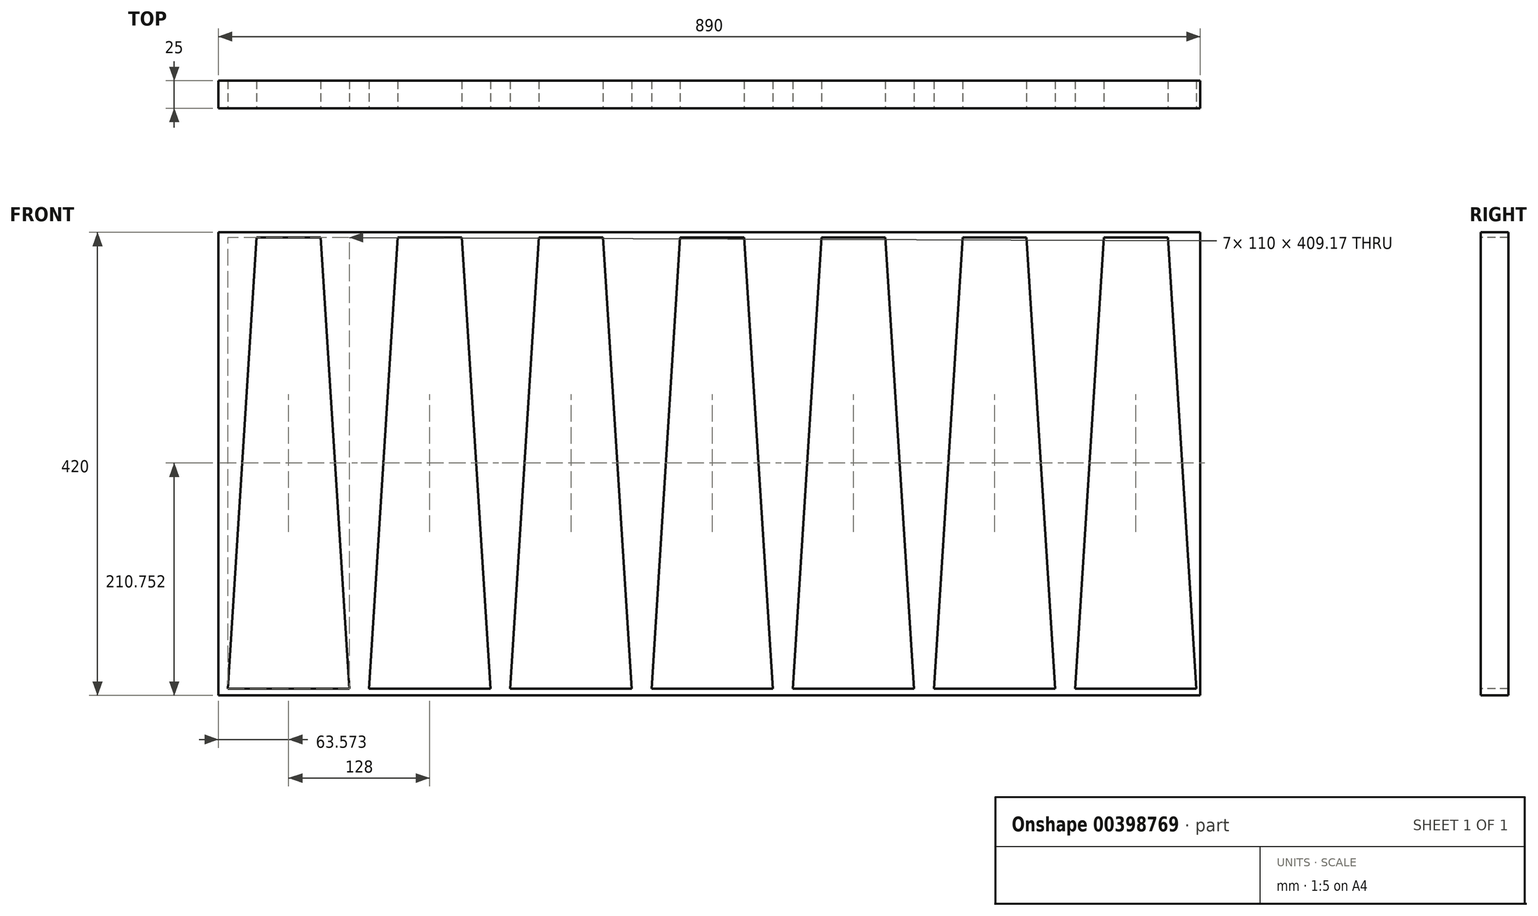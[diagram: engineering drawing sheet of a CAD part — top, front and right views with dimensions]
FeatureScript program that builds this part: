
annotation { "Feature Type Name" : "Feature", "Feature Type Description" : "" }
export const myFeature = defineFeature(function(context is Context, id is Id, definition is map)
    precondition{}
    {
        {
            var Q0;
            Q0=qCreatedBy(makeId("Front.planeOp"),FACE);
            var sketch = newSketch(context, id + "F0", { "sketchPlane" : qUnion([Q0])});
            skLineSegment(sketch, "E0.bottom", {"start": v(445, -210) * mm, "end": v(-445, -210) * mm});
            skLineSegment(sketch, "E0.top", {"start": v(445, 210) * mm, "end": v(-445, 210) * mm});
            skLineSegment(sketch, "E0.left", {"start": v(445, -210) * mm, "end": v(445, 210) * mm});
            skLineSegment(sketch, "E0.right", {"start": v(-445, -210) * mm, "end": v(-445, 210) * mm});
            skPoint(sketch, "E0.middle", {"position": v(0, 0) * mm});
            skSolve(sketch);
        }
        {
            var Q0;
            Q0 = qSketchRegion(id + "F0", true);
            extrude(context, id + "F1", {"entities" : qUnion([Q0]), "depth" : 25 * mm});
        }
        {
            var Q0;
            Q0=makeQuery(id+"F1.opExtrude","CAP_FACE",FACE,{"disambiguationData":[OSD([sQuery(id+"F0.wireOp",EDGE,"E0.bottom"),sQuery(id+"F0.wireOp",EDGE,"E0.top"),sQuery(id+"F0.wireOp",EDGE,"E0.left"),sQuery(id+"F0.wireOp",EDGE,"E0.right")])],"isStart":false});
            var sketch = newSketch(context, id + "F2", { "sketchPlane" : qUnion([Q0])});
            skLineSegment(sketch, "E1", {"start": v(-381.43, -203.83) * mm, "end": v(-326.43, -203.83) * mm});
            skLineSegment(sketch, "E2", {"start": v(-326.43, -203.83) * mm, "end": v(-352.43, 205.34) * mm});
            skLineSegment(sketch, "E3", {"start": v(-352.43, 205.34) * mm, "end": v(-381.43, 205.34) * mm});
            skLineSegment(sketch, "E4", {"start": v(-381.43, 143.69) * mm, "end": v(-381.43, -293.33) * mm, "construction": true});
            skLineSegment(sketch, "E5.MirrorCS", {"start": v(-410.43, 205.34) * mm, "end": v(-381.43, 205.34) * mm});
            skLineSegment(sketch, "E6.MirrorCS", {"start": v(-436.43, -203.83) * mm, "end": v(-410.43, 205.34) * mm});
            skLineSegment(sketch, "E7.MirrorCS", {"start": v(-381.43, -203.83) * mm, "end": v(-436.43, -203.83) * mm});
            skLineSegment(sketch, "E8.1.0.0", {"start": v(-253.43, 143.69) * mm, "end": v(-253.43, -293.33) * mm, "construction": true});
            skLineSegment(sketch, "E8.1.0.1", {"start": v(-253.43, -203.83) * mm, "end": v(-198.43, -203.83) * mm});
            skLineSegment(sketch, "E8.1.0.2", {"start": v(-198.43, -203.83) * mm, "end": v(-224.43, 205.34) * mm});
            skLineSegment(sketch, "E8.1.0.3", {"start": v(-253.43, -203.83) * mm, "end": v(-308.43, -203.83) * mm});
            skLineSegment(sketch, "E8.1.0.4", {"start": v(-308.43, -203.83) * mm, "end": v(-282.43, 205.34) * mm});
            skLineSegment(sketch, "E8.1.0.5", {"start": v(-282.43, 205.34) * mm, "end": v(-253.43, 205.34) * mm});
            skLineSegment(sketch, "E8.1.0.6", {"start": v(-224.43, 205.34) * mm, "end": v(-253.43, 205.34) * mm});
            skLineSegment(sketch, "E8.2.0.0", {"start": v(-125.43, 143.69) * mm, "end": v(-125.43, -293.33) * mm, "construction": true});
            skLineSegment(sketch, "E8.2.0.1", {"start": v(-125.43, -203.83) * mm, "end": v(-70.43, -203.83) * mm});
            skLineSegment(sketch, "E8.2.0.2", {"start": v(-70.43, -203.83) * mm, "end": v(-96.43, 205.34) * mm});
            skLineSegment(sketch, "E8.2.0.3", {"start": v(-125.43, -203.83) * mm, "end": v(-180.43, -203.83) * mm});
            skLineSegment(sketch, "E8.2.0.4", {"start": v(-180.43, -203.83) * mm, "end": v(-154.43, 205.34) * mm});
            skLineSegment(sketch, "E8.2.0.5", {"start": v(-154.43, 205.34) * mm, "end": v(-125.43, 205.34) * mm});
            skLineSegment(sketch, "E8.2.0.6", {"start": v(-96.43, 205.34) * mm, "end": v(-125.43, 205.34) * mm});
            skLineSegment(sketch, "E8.3.0.0", {"start": v(2.57, 143.69) * mm, "end": v(2.57, -293.33) * mm, "construction": true});
            skLineSegment(sketch, "E8.3.0.1", {"start": v(2.57, -203.83) * mm, "end": v(57.57, -203.83) * mm});
            skLineSegment(sketch, "E8.3.0.2", {"start": v(57.57, -203.83) * mm, "end": v(31.57, 205.34) * mm});
            skLineSegment(sketch, "E8.3.0.3", {"start": v(2.57, -203.83) * mm, "end": v(-52.43, -203.83) * mm});
            skLineSegment(sketch, "E8.3.0.4", {"start": v(-52.43, -203.83) * mm, "end": v(-26.43, 205.34) * mm});
            skLineSegment(sketch, "E8.3.0.5", {"start": v(-26.43, 205.34) * mm, "end": v(2.57, 205.34) * mm});
            skLineSegment(sketch, "E8.3.0.6", {"start": v(31.57, 205.34) * mm, "end": v(2.57, 205.34) * mm});
            skLineSegment(sketch, "E8.4.0.0", {"start": v(130.57, 143.69) * mm, "end": v(130.57, -293.33) * mm, "construction": true});
            skLineSegment(sketch, "E8.4.0.1", {"start": v(130.57, -203.83) * mm, "end": v(185.57, -203.83) * mm});
            skLineSegment(sketch, "E8.4.0.2", {"start": v(185.57, -203.83) * mm, "end": v(159.57, 205.34) * mm});
            skLineSegment(sketch, "E8.4.0.3", {"start": v(130.57, -203.83) * mm, "end": v(75.57, -203.83) * mm});
            skLineSegment(sketch, "E8.4.0.4", {"start": v(75.57, -203.83) * mm, "end": v(101.57, 205.34) * mm});
            skLineSegment(sketch, "E8.4.0.5", {"start": v(101.57, 205.34) * mm, "end": v(130.57, 205.34) * mm});
            skLineSegment(sketch, "E8.4.0.6", {"start": v(159.57, 205.34) * mm, "end": v(130.57, 205.34) * mm});
            skLineSegment(sketch, "E8.5.0.0", {"start": v(258.57, 143.69) * mm, "end": v(258.57, -293.33) * mm, "construction": true});
            skLineSegment(sketch, "E8.5.0.1", {"start": v(258.57, -203.83) * mm, "end": v(313.57, -203.83) * mm});
            skLineSegment(sketch, "E8.5.0.2", {"start": v(313.57, -203.83) * mm, "end": v(287.57, 205.34) * mm});
            skLineSegment(sketch, "E8.5.0.3", {"start": v(258.57, -203.83) * mm, "end": v(203.57, -203.83) * mm});
            skLineSegment(sketch, "E8.5.0.4", {"start": v(203.57, -203.83) * mm, "end": v(229.57, 205.34) * mm});
            skLineSegment(sketch, "E8.5.0.5", {"start": v(229.57, 205.34) * mm, "end": v(258.57, 205.34) * mm});
            skLineSegment(sketch, "E8.5.0.6", {"start": v(287.57, 205.34) * mm, "end": v(258.57, 205.34) * mm});
            skLineSegment(sketch, "E8.6.0.0", {"start": v(386.57, 143.69) * mm, "end": v(386.57, -293.33) * mm, "construction": true});
            skLineSegment(sketch, "E8.6.0.1", {"start": v(386.57, -203.83) * mm, "end": v(441.57, -203.83) * mm});
            skLineSegment(sketch, "E8.6.0.2", {"start": v(441.57, -203.83) * mm, "end": v(415.57, 205.34) * mm});
            skLineSegment(sketch, "E8.6.0.3", {"start": v(386.57, -203.83) * mm, "end": v(331.57, -203.83) * mm});
            skLineSegment(sketch, "E8.6.0.4", {"start": v(331.57, -203.83) * mm, "end": v(357.57, 205.34) * mm});
            skLineSegment(sketch, "E8.6.0.5", {"start": v(357.57, 205.34) * mm, "end": v(386.57, 205.34) * mm});
            skLineSegment(sketch, "E8.6.0.6", {"start": v(415.57, 205.34) * mm, "end": v(386.57, 205.34) * mm});
            skLineSegment(sketch, "E8.direction1", {"start": v(-381.43, -293.33) * mm, "end": v(-253.43, -293.33) * mm, "construction": true});
            skSolve(sketch);
        }
        {
            var Q0;
            Q0=makeQuery(id+"F2.imprint","IMPRINT",FACE,{"disambiguationData":[TD([[makeQuery(id+"F2.imprint","IMPRINT",EDGE,{"derivedFrom":sQuery(id+"F2.wireOp",EDGE,"E1")}),1.0]])]});
            var Q1;
            Q1=makeQuery(id+"F2.imprint","IMPRINT",FACE,{"disambiguationData":[TD([[makeQuery(id+"F2.imprint","IMPRINT",EDGE,{"derivedFrom":sQuery(id+"F2.wireOp",EDGE,"E8.1.0.1")}),1.0]])]});
            var Q2;
            Q2=makeQuery(id+"F2.imprint","IMPRINT",FACE,{"disambiguationData":[TD([[makeQuery(id+"F2.imprint","IMPRINT",EDGE,{"derivedFrom":sQuery(id+"F2.wireOp",EDGE,"E8.2.0.1")}),1.0]])]});
            var Q3;
            Q3=makeQuery(id+"F2.imprint","IMPRINT",FACE,{"disambiguationData":[TD([[makeQuery(id+"F2.imprint","IMPRINT",EDGE,{"derivedFrom":sQuery(id+"F2.wireOp",EDGE,"E8.3.0.1")}),1.0]])]});
            var Q4;
            Q4=makeQuery(id+"F2.imprint","IMPRINT",FACE,{"disambiguationData":[TD([[makeQuery(id+"F2.imprint","IMPRINT",EDGE,{"derivedFrom":sQuery(id+"F2.wireOp",EDGE,"E8.4.0.1")}),1.0]])]});
            var Q5;
            Q5=makeQuery(id+"F2.imprint","IMPRINT",FACE,{"disambiguationData":[TD([[makeQuery(id+"F2.imprint","IMPRINT",EDGE,{"derivedFrom":sQuery(id+"F2.wireOp",EDGE,"E8.5.0.1")}),1.0]])]});
            var Q6;
            Q6=makeQuery(id+"F2.imprint","IMPRINT",FACE,{"disambiguationData":[TD([[makeQuery(id+"F2.imprint","IMPRINT",EDGE,{"derivedFrom":sQuery(id+"F2.wireOp",EDGE,"E8.6.0.1")}),1.0]])]});
            extrude(context, id + "F3", {"entities" : qUnion([Q0, Q1, Q2, Q3, Q4, Q5, Q6]), "operationType" : NewBodyOperationType.REMOVE, "oppositeDirection" : true, "depth" : 25 * mm});
        }
    });
